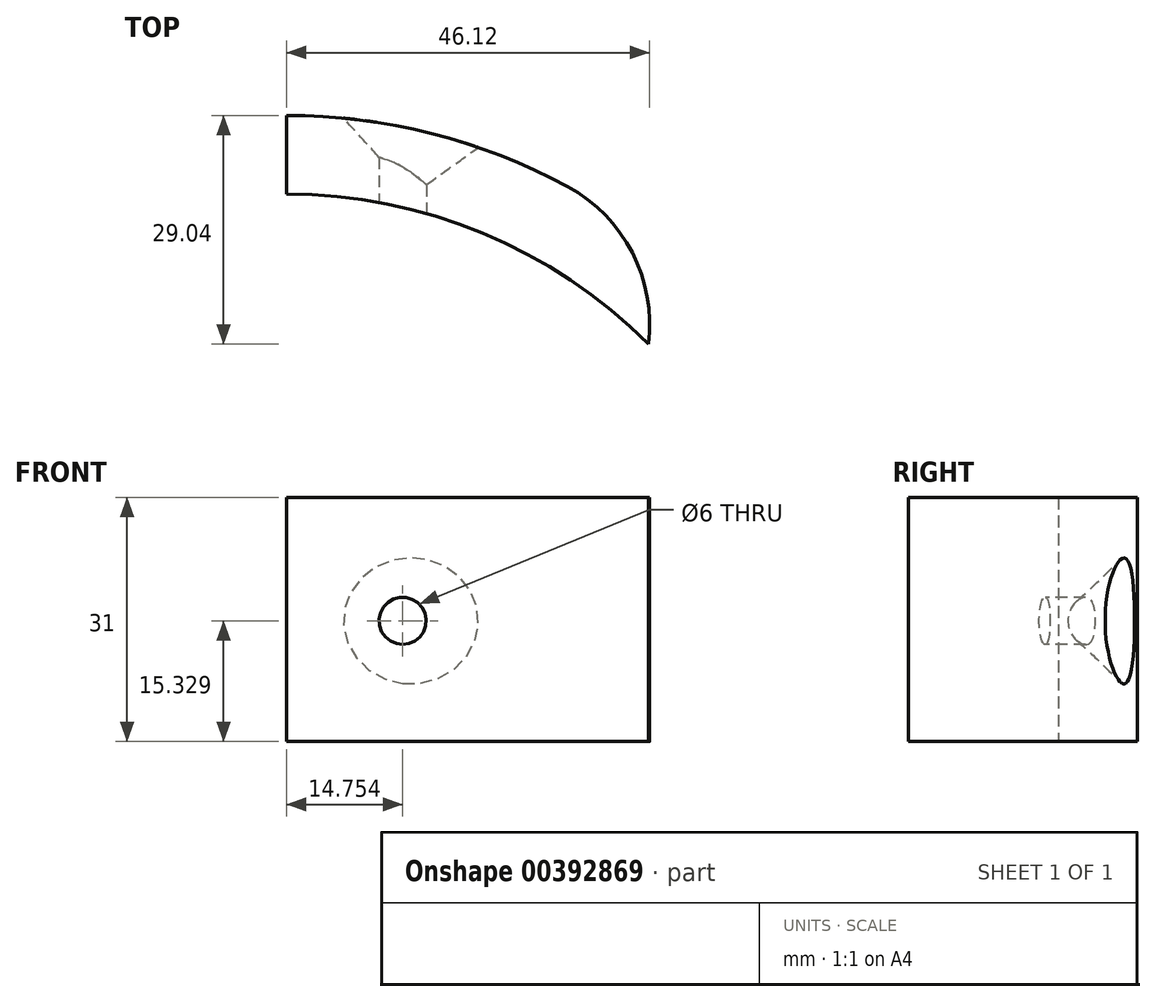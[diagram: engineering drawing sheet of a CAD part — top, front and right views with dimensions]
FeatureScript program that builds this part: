
annotation { "Feature Type Name" : "Feature", "Feature Type Description" : "" }
export const myFeature = defineFeature(function(context is Context, id is Id, definition is map)
    precondition{}
    {
        {
            var Q0;
            Q0=qCreatedBy(makeId("Top.planeOp"),FACE);
            var sketch = newSketch(context, id + "F0", { "sketchPlane" : qUnion([Q0])});
            skArc(sketch, "E0", {"start": v(0, 75) * mm, "mid": v(53.03, 53.03) * mm, "end": v(75, 0) * mm});
            skArc(sketch, "E1.0", {"start": v(0, 65) * mm, "mid": v(45.96, 45.96) * mm, "end": v(65, 0) * mm});
            skLineSegment(sketch, "E2", {"start": v(0, 75) * mm, "end": v(0, 65) * mm});
            skLineSegment(sketch, "E3", {"start": v(53.03, 53.03) * mm, "end": v(45.96, 45.96) * mm});
            skSolve(sketch);
        }
        {
            var Q0;
            {var subQ0=sQuery(id+"F0.wireOp",EDGE,"E2");Q0=makeQuery(id+"F0.imprint","IMPRINT",FACE,{"disambiguationData":[TD([[makeQuery(id+"F0.imprint","IMPRINT",EDGE,{"derivedFrom":subQ0}),1.0]])]});}
            extrude(context, id + "F1", {"entities" : qUnion([Q0]), "depth" : 31 * mm});
        }
        {
            var Q0;
            Q0=makeQuery(id+"F1.opExtrude","SWEPT_EDGE",EDGE,{"disambiguationData":[OSD([sQuery(id+"F0.wireOp",EDGE,"E0"),sQuery(id+"F0.wireOp",EDGE,"E3")])]});
            fillet(context, id + "F2", {"entities" : qUnion([Q0]), "radius" : 19.9 * mm, "tangentPropagation" : true, "allowEdgeOverflow" : false});
        }
        {
            var Q0;
            Q0=qCreatedBy(makeId("Front.planeOp"),FACE);
            var sketch = newSketch(context, id + "F3", { "sketchPlane" : qUnion([Q0])});
            skCircle(sketch, "E4", {"center": v(14.75, 15.33) * mm, "radius": 3 * mm});
            skSolve(sketch);
        }
        {
            var Q0;
            Q0 = qSketchRegion(id + "F3", true);
            extrude(context, id + "F4", {"entities" : qUnion([Q0]), "operationType" : NewBodyOperationType.REMOVE, "oppositeDirection" : true, "depth" : 125.9 * mm});
        }
        {
            var Q0;
            Q0=makeQuery(id+"F4.boolean.opBoolean","INTERSECT",EDGE,{"derivedFrom":[makeQuery(id+"F1.opExtrude","SWEPT_FACE",FACE,{"disambiguationData":[OSD([sQuery(id+"F0.wireOp",EDGE,"E0")])]}),makeQuery(id+"F4.opExtrude","SWEPT_FACE",FACE,{"disambiguationData":[OSD([sQuery(id+"F3.wireOp",EDGE,"E4")])]})]});
            chamfer(context, id + "F5", {"entities" : qUnion([Q0]), "width" : 5 * mm, "tangentPropagation" : true});
        }
    });
